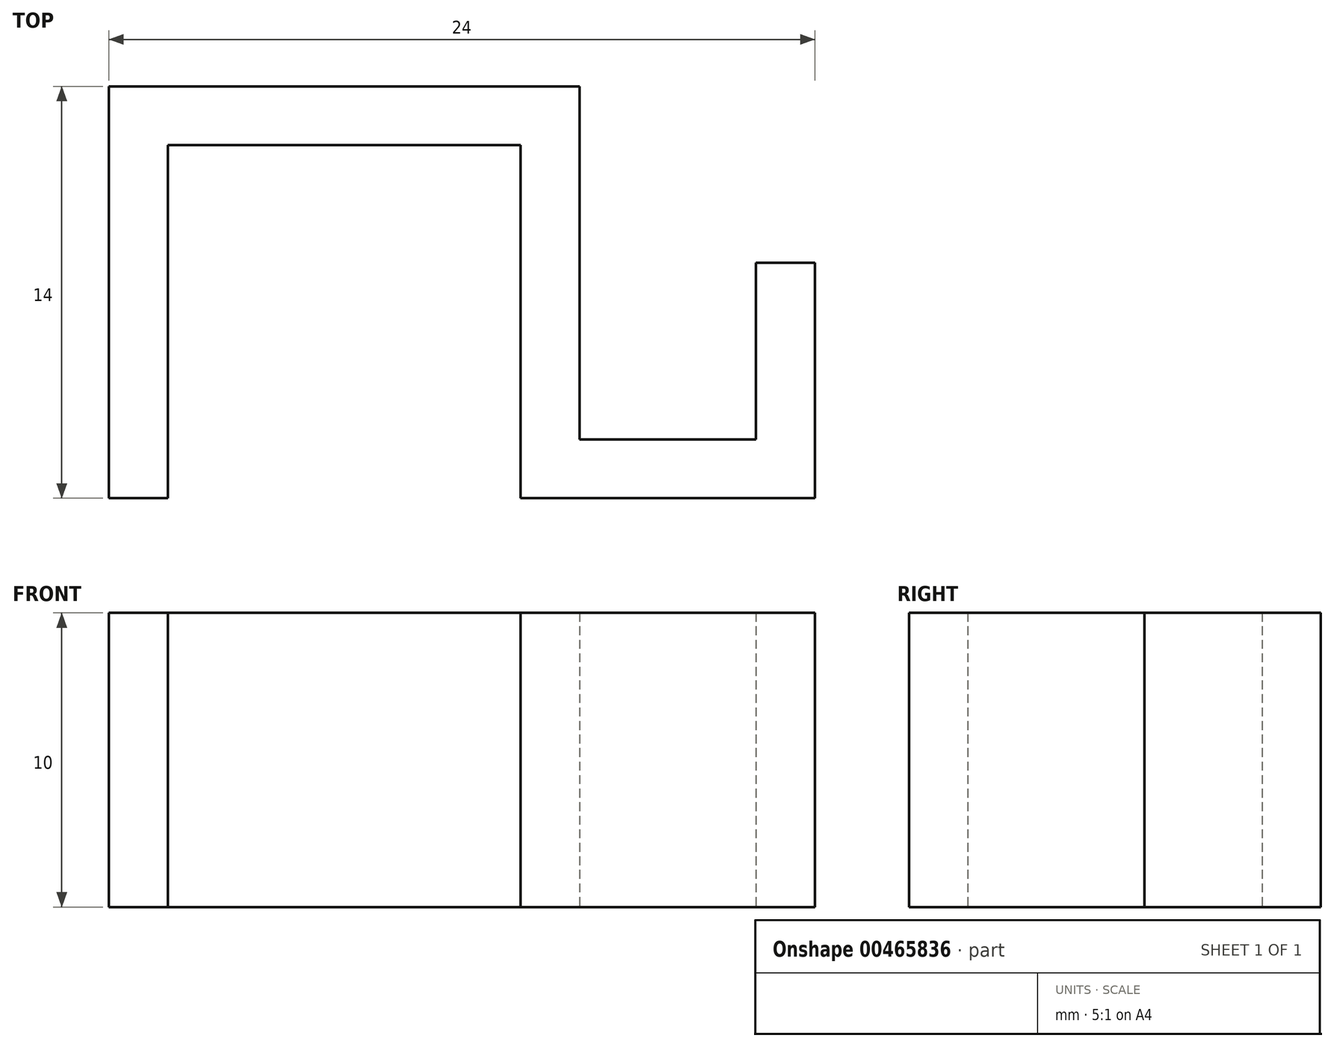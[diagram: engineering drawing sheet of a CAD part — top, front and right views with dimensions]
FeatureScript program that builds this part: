
annotation { "Feature Type Name" : "Feature", "Feature Type Description" : "" }
export const myFeature = defineFeature(function(context is Context, id is Id, definition is map)
    precondition{}
    {
        {
            var Q0;
            Q0=qCreatedBy(makeId("Top.planeOp"),FACE);
            var sketch = newSketch(context, id + "F0", { "sketchPlane" : qUnion([Q0])});
            skLineSegment(sketch, "E0", {"start": v(0, 0) * mm, "end": v(0, 12) * mm});
            skLineSegment(sketch, "E1", {"start": v(0, 12) * mm, "end": v(12, 12) * mm});
            skLineSegment(sketch, "E2", {"start": v(12, 12) * mm, "end": v(12, 0) * mm});
            skLineSegment(sketch, "E3.0", {"start": v(14, 14) * mm, "end": v(14, 2) * mm});
            skLineSegment(sketch, "E3.1", {"start": v(-2, 14) * mm, "end": v(14, 14) * mm});
            skLineSegment(sketch, "E3.2", {"start": v(-2, 0) * mm, "end": v(-2, 14) * mm});
            skLineSegment(sketch, "E4", {"start": v(-2, 0) * mm, "end": v(0, 0) * mm});
            skLineSegment(sketch, "E5", {"start": v(12, 0) * mm, "end": v(14, 0) * mm});
            skLineSegment(sketch, "E6", {"start": v(14, 0) * mm, "end": v(22, 0) * mm});
            skLineSegment(sketch, "E7", {"start": v(22, 0) * mm, "end": v(22, 8) * mm});
            skLineSegment(sketch, "E8.0", {"start": v(20, 2) * mm, "end": v(20, 8) * mm});
            skLineSegment(sketch, "E8.1", {"start": v(14, 2) * mm, "end": v(20, 2) * mm});
            skLineSegment(sketch, "E9", {"start": v(20, 8) * mm, "end": v(22, 8) * mm});
            skSolve(sketch);
        }
        {
            var Q0;
            Q0 = qSketchRegion(id + "F0", true);
            extrude(context, id + "F1", {"entities" : qUnion([Q0]), "depth" : 10 * mm});
        }
    });
